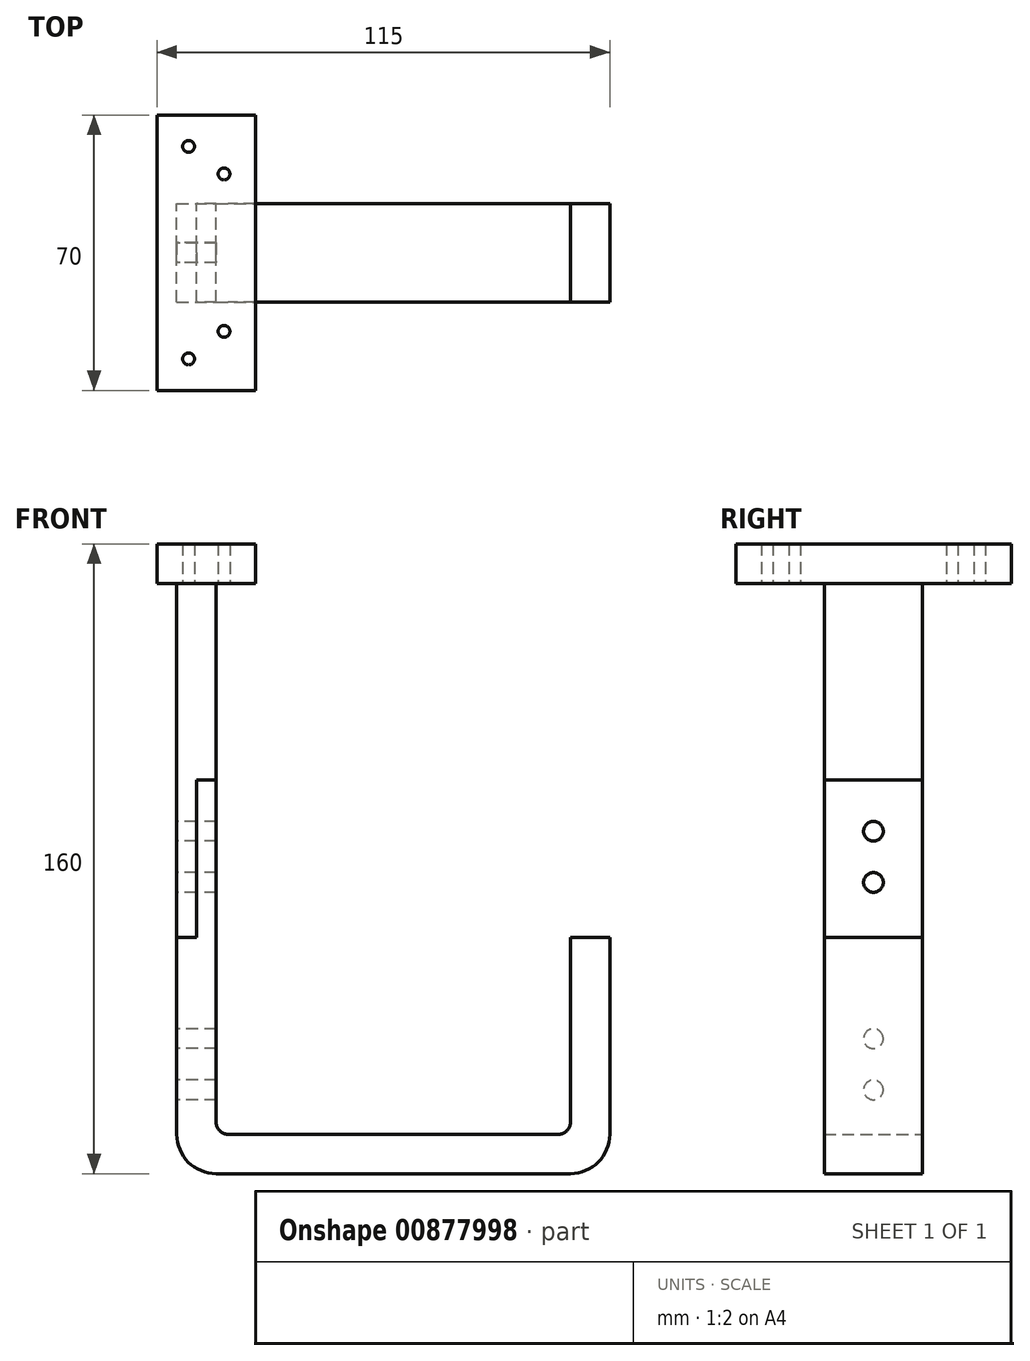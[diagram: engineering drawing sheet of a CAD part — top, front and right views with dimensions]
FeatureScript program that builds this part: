
annotation { "Feature Type Name" : "Feature", "Feature Type Description" : "" }
export const myFeature = defineFeature(function(context is Context, id is Id, definition is map)
    precondition{}
    {
        {
            var Q0;
            Q0=qCreatedBy(makeId("Front.planeOp"),FACE);
            var sketch = newSketch(context, id + "F0", { "sketchPlane" : qUnion([Q0])});
            skLineSegment(sketch, "E0", {"start": v(39.6, 12.87) * mm, "end": v(-60.4, 12.87) * mm});
            skLineSegment(sketch, "E1.0", {"start": v(39.6, 22.87) * mm, "end": v(-60.4, 22.87) * mm});
            skLineSegment(sketch, "E2", {"start": v(-60.4, 22.87) * mm, "end": v(-60.4, 12.87) * mm});
            skLineSegment(sketch, "E3", {"start": v(39.6, 22.87) * mm, "end": v(39.6, 12.87) * mm});
            skLineSegment(sketch, "E4", {"start": v(-60.4, 22.87) * mm, "end": v(-60.4, 112.87) * mm});
            skLineSegment(sketch, "E5", {"start": v(-60.4, 112.87) * mm, "end": v(-70.4, 112.87) * mm});
            skLineSegment(sketch, "E6", {"start": v(-70.4, 112.87) * mm, "end": v(-70.4, 12.87) * mm});
            skLineSegment(sketch, "E7", {"start": v(-70.4, 12.87) * mm, "end": v(-60.4, 12.87) * mm});
            skLineSegment(sketch, "E8", {"start": v(-65.4, 112.87) * mm, "end": v(-65.4, 72.87) * mm});
            skLineSegment(sketch, "E9", {"start": v(-70.4, 72.87) * mm, "end": v(-65.4, 72.87) * mm});
            skLineSegment(sketch, "E10", {"start": v(-70.4, 112.87) * mm, "end": v(-70.4, 162.87) * mm});
            skLineSegment(sketch, "E11", {"start": v(-70.4, 162.87) * mm, "end": v(-60.4, 162.87) * mm});
            skLineSegment(sketch, "E12", {"start": v(-60.4, 162.87) * mm, "end": v(-60.4, 112.87) * mm});
            skLineSegment(sketch, "E13", {"start": v(39.6, 22.87) * mm, "end": v(39.6, 72.87) * mm});
            skLineSegment(sketch, "E14", {"start": v(29.6, 72.87) * mm, "end": v(29.6, 22.87) * mm});
            skLineSegment(sketch, "E15", {"start": v(29.6, 72.87) * mm, "end": v(39.6, 72.87) * mm});
            skSolve(sketch);
        }
        {
            var Q0;
            Q0=makeQuery(id+"F0.imprint","IMPRINT",FACE,{"disambiguationData":[TD([[makeQuery(id+"F0.imprint","IMPRINT",EDGE,{"derivedFrom":sQuery(id+"F0.wireOp",EDGE,"E2")}),-1.0]])]});
            var Q1;
            Q1=makeQuery(id+"F0.imprint","IMPRINT",FACE,{"disambiguationData":[TD([[makeQuery(id+"F0.imprint","IMPRINT",EDGE,{"derivedFrom":sQuery(id+"F0.wireOp",EDGE,"E0")}),-1.0]])]});
            var Q2;
            {var subQ0=sQuery(id+"F0.wireOp",EDGE,"E13");Q2=makeQuery(id+"F0.imprint","IMPRINT",FACE,{"disambiguationData":[TD([[makeQuery(id+"F0.imprint","IMPRINT",EDGE,{"derivedFrom":subQ0}),1.0]])]});}
            extrude(context, id + "F1", {"entities" : qUnion([Q0, Q1, Q2]), "endBound" : BoundingType.SYMMETRIC, "depth" : 25 * mm, "offsetDistance" : 25 * mm});
        }
        {
            var Q0;
            {var subQ0=sQuery(id+"F0.wireOp",EDGE,"E10");Q0=makeQuery(id+"F0.imprint","IMPRINT",FACE,{"disambiguationData":[TD([[makeQuery(id+"F0.imprint","IMPRINT",EDGE,{"derivedFrom":subQ0}),-1.0]])]});}
            var Q1;
            {var subQ3=sQuery(id+"F0.wireOp",EDGE,"E8");Q1=makeQuery(id+"F0.imprint","IMPRINT",FACE,{"disambiguationData":[TD([[makeQuery(id+"F0.imprint","IMPRINT",EDGE,{"derivedFrom":subQ3}),-1.0]])]});}
            extrude(context, id + "F2", {"entities" : qUnion([Q0, Q1]), "endBound" : BoundingType.SYMMETRIC, "depth" : 25 * mm, "offsetDistance" : 25 * mm});
        }
        {
            var Q0;
            Q0=makeQuery(id+"F2.opExtrude","SWEPT_FACE",FACE,{"disambiguationData":[OSD([sQuery(id+"F0.wireOp",EDGE,"E6"),sQuery(id+"F0.wireOp",EDGE,"E10")])]});
            var sketch = newSketch(context, id + "F3", { "sketchPlane" : qUnion([Q0])});
            skPoint(sketch, "E16", {"position": v(0, 99.87) * mm});
            skPoint(sketch, "E17", {"position": v(0, 86.87) * mm});
            skPoint(sketch, "E18", {"position": v(0, 34.15) * mm});
            skPoint(sketch, "E19", {"position": v(0, 47.15) * mm});
            skSolve(sketch);
        }
        {
            var Q0;
            Q0=sQuery(id+"F3.wireOp",VERTEX,"E16");
            var Q1;
            Q1=sQuery(id+"F3.wireOp",VERTEX,"E17");
            var Q2;
            Q2=sQuery(id+"F3.wireOp",VERTEX,"E19");
            var Q3;
            Q3=sQuery(id+"F3.wireOp",VERTEX,"E18");
            var Q4;
            Q4=makeQuery(id+"F1.opExtrude","SWEPT_BODY",BODY,{"disambiguationData":[OSD([sQuery(id+"F0.wireOp",EDGE,"E0"),sQuery(id+"F0.wireOp",EDGE,"E1.0"),sQuery(id+"F0.wireOp",EDGE,"E3"),sQuery(id+"F0.wireOp",EDGE,"E4"),sQuery(id+"F0.wireOp",EDGE,"E5"),sQuery(id+"F0.wireOp",EDGE,"E6"),sQuery(id+"F0.wireOp",EDGE,"E7"),sQuery(id+"F0.wireOp",EDGE,"E8"),sQuery(id+"F0.wireOp",EDGE,"E9"),sQuery(id+"F0.wireOp",EDGE,"E13"),sQuery(id+"F0.wireOp",EDGE,"E14"),sQuery(id+"F0.wireOp",EDGE,"E15")])]});
            var Q5;
            Q5=makeQuery(id+"F2.opExtrude","SWEPT_BODY",BODY,{"disambiguationData":[OSD([sQuery(id+"F0.wireOp",EDGE,"E5"),sQuery(id+"F0.wireOp",EDGE,"E6"),sQuery(id+"F0.wireOp",EDGE,"E8"),sQuery(id+"F0.wireOp",EDGE,"E9"),sQuery(id+"F0.wireOp",EDGE,"E10"),sQuery(id+"F0.wireOp",EDGE,"E11"),sQuery(id+"F0.wireOp",EDGE,"E12")])]});
            hole(context, id + "F4", {"style" : HoleStyle.SIMPLE, "endStyle" : HoleEndStyle.BLIND, "holeDiameter" : 5 * mm, "majorDiameter" : 5 * mm, "holeDepth" : 30 * mm, "isTappedThrough" : true, "tappedDepth" : 12 * mm, "tapClearance" : 3, "locations" : qUnion([Q0, Q1, Q2, Q3]), "scope" : qUnion([Q4, Q5])});
        }
        {
            var Q0;
            Q0=makeQuery(id+"F2.opExtrude","SWEPT_FACE",FACE,{"disambiguationData":[OSD([sQuery(id+"F0.wireOp",EDGE,"E11")])]});
            var sketch = newSketch(context, id + "F5", { "sketchPlane" : qUnion([Q0])});
            skLineSegment(sketch, "E20.bottom", {"start": v(-75.4, 35) * mm, "end": v(-50.4, 35) * mm});
            skLineSegment(sketch, "E20.top", {"start": v(-75.4, -35) * mm, "end": v(-50.4, -35) * mm});
            skLineSegment(sketch, "E20.left", {"start": v(-75.4, 35) * mm, "end": v(-75.4, -35) * mm});
            skLineSegment(sketch, "E20.right", {"start": v(-50.4, 35) * mm, "end": v(-50.4, -35) * mm});
            skPoint(sketch, "E21", {"position": v(-67.4, 27) * mm});
            skPoint(sketch, "E22", {"position": v(-58.4, 20) * mm});
            skPoint(sketch, "E23", {"position": v(-58.4, -20) * mm});
            skPoint(sketch, "E24", {"position": v(-67.4, -27) * mm});
            skSolve(sketch);
        }
        {
            var Q0;
            Q0=makeQuery(id+"F5.imprint","IMPRINT",FACE,{"disambiguationData":[TD([[makeQuery(id+"F5.imprint","IMPRINT",EDGE,{"derivedFrom":sQuery(id+"F5.wireOp",EDGE,"E20.bottom")}),-1.0]])]});
            var Q1;
            {var subQ0=sQuery(id+"F0.wireOp",EDGE,"E11");Q1=makeQuery(id+"F5.imprint","IMPRINT",FACE,{"disambiguationData":[TD([[makeQuery(id+"F5.imprint","IMPRINT",EDGE,{"derivedFrom":makeQuery(id+"F2.opExtrude","CAP_EDGE",EDGE,{"disambiguationData":[OSD([subQ0])],"isStart":true})}),-1.0]])]});}
            extrude(context, id + "F6", {"entities" : qUnion([Q0, Q1]), "operationType" : NewBodyOperationType.ADD, "depth" : 10 * mm, "offsetDistance" : 25 * mm});
        }
        {
            var Q0;
            Q0=sQuery(id+"F5.wireOp",VERTEX,"E22");
            var Q1;
            Q1=sQuery(id+"F5.wireOp",VERTEX,"E21");
            var Q2;
            Q2=sQuery(id+"F5.wireOp",VERTEX,"E23");
            var Q3;
            Q3=sQuery(id+"F5.wireOp",VERTEX,"E24");
            var Q4;
            Q4=makeQuery(id+"F2.opExtrude","SWEPT_BODY",BODY,{"disambiguationData":[OSD([sQuery(id+"F0.wireOp",EDGE,"E5"),sQuery(id+"F0.wireOp",EDGE,"E6"),sQuery(id+"F0.wireOp",EDGE,"E8"),sQuery(id+"F0.wireOp",EDGE,"E9"),sQuery(id+"F0.wireOp",EDGE,"E10"),sQuery(id+"F0.wireOp",EDGE,"E11"),sQuery(id+"F0.wireOp",EDGE,"E12")])]});
            hole(context, id + "F7", {"style" : HoleStyle.SIMPLE, "endStyle" : HoleEndStyle.THROUGH, "oppositeDirection" : true, "holeDiameter" : 3 * mm, "majorDiameter" : 5 * mm, "isTappedThrough" : true, "tappedDepth" : 12 * mm, "tapClearance" : 3, "locations" : qUnion([Q0, Q1, Q2, Q3]), "scope" : qUnion([Q4])});
        }
        {
            var Q0;
            Q0=makeQuery(id+"F1.opExtrude","SWEPT_EDGE",EDGE,{"disambiguationData":[OSD([sQuery(id+"F0.wireOp",EDGE,"E6"),sQuery(id+"F0.wireOp",EDGE,"E7")])]});
            var Q1;
            Q1=makeQuery(id+"F1.opExtrude","SWEPT_EDGE",EDGE,{"disambiguationData":[OSD([sQuery(id+"F0.wireOp",EDGE,"E0"),sQuery(id+"F0.wireOp",EDGE,"E3")])]});
            fillet(context, id + "F8", {"entities" : qUnion([Q0, Q1]), "radius" : 10 * mm, "tangentPropagation" : true, "allowEdgeOverflow" : false});
        }
        {
            var Q0;
            Q0=makeQuery(id+"F1.opExtrude","SWEPT_EDGE",EDGE,{"disambiguationData":[OSD([sQuery(id+"F0.wireOp",EDGE,"E1.0"),sQuery(id+"F0.wireOp",EDGE,"E14")])]});
            var Q1;
            Q1=makeQuery(id+"F1.opExtrude","SWEPT_EDGE",EDGE,{"disambiguationData":[OSD([sQuery(id+"F0.wireOp",EDGE,"E1.0"),sQuery(id+"F0.wireOp",EDGE,"E2"),sQuery(id+"F0.wireOp",EDGE,"E4")])]});
            fillet(context, id + "F9", {"entities" : qUnion([Q0, Q1]), "radius" : 3 * mm, "tangentPropagation" : true, "allowEdgeOverflow" : false});
        }
    });
